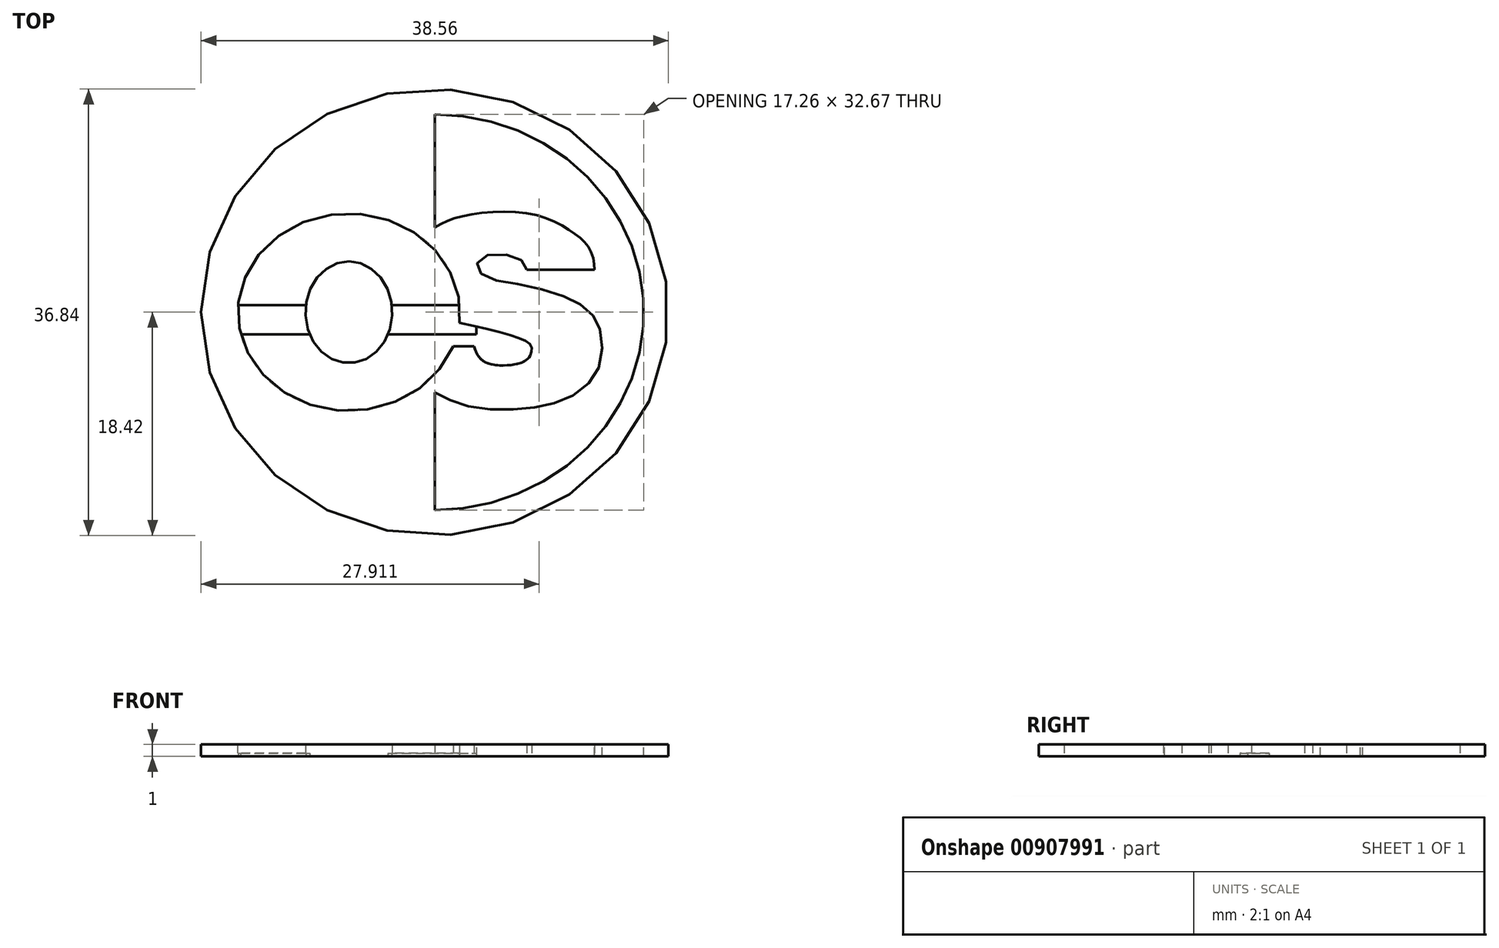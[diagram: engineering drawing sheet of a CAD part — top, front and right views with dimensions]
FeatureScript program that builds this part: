
annotation { "Feature Type Name" : "Feature", "Feature Type Description" : "" }
export const myFeature = defineFeature(function(context is Context, id is Id, definition is map)
    precondition{}
    {
        {
            var Q0;
            Q0=qCreatedBy(makeId("Top.planeOp"),FACE);
            var sketch = newSketch(context, id + "F0", { "sketchPlane" : qUnion([Q0])});
            skEllipse(sketch, "E0", {"center": v(0, 0) * mm, "majorRadius": 18.42 * mm, "minorRadius": 19.28 * mm, "majorAxis": v(0, 1)});
            skEllipticalArc(sketch, "E1", {});
            skEllipse(sketch, "E2", {"center": v(-7.08, 0) * mm, "majorRadius": 4.2 * mm, "minorRadius": 3.58 * mm, "majorAxis": v(0, 1)});
            skEllipticalArc(sketch, "E3", {});
            skLineSegment(sketch, "E4", {"start": v(0, 16.34) * mm, "end": v(0, 6.99) * mm});
            skLineSegment(sketch, "E5", {"start": v(0, -6.61) * mm, "end": v(0, -16.34) * mm});
            skFitSpline(sketch, "E6", {"points": [v(0, 6.99) * mm, v(2.69, 8.01) * mm, v(8.28, 8.04) * mm, v(11.51, 6.51) * mm, v(12.8, 5.2) * mm, v(13.2, 3.52) * mm], "startDerivative": vector(11.6, 7.03) * mm, "endDerivative": vector(-0.27, -9.65) * mm});
            skLineSegment(sketch, "E7", {"start": v(13.2, 3.52) * mm, "end": v(7.61, 3.52) * mm});
            skFitSpline(sketch, "E8", {"points": [v(7.61, 3.52) * mm, v(7.34, 4.12) * mm, v(6.38, 4.64) * mm, v(4.4, 4.73) * mm, v(3.55, 4.12) * mm, v(3.55, 3.52) * mm, v(4.5, 2.8) * mm, v(6.82, 2.34) * mm, v(10.06, 1.51) * mm, v(11.98, 0.66) * mm, v(13.13, -0.38) * mm, v(13.68, -1.53) * mm, v(13.74, -3.81) * mm, v(13, -5.54) * mm, v(11.26, -6.97) * mm, v(9.1, -7.71) * mm, v(6.68, -8.01) * mm, v(3.74, -7.93) * mm, v(1.52, -7.35) * mm, v(0, -6.61) * mm], "startDerivative": vector(-5.92, 19.87) * mm, "endDerivative": vector(-28.15, 15.2) * mm});
            skFitSpline(sketch, "E9", {"points": [v(2.03, -0.88) * mm, v(7.2, -2.24) * mm, v(7.99, -2.84) * mm, v(7.94, -3.44) * mm, v(7.65, -3.89) * mm, v(7.16, -4.16) * mm, v(6.1, -4.37) * mm, v(4.53, -4.26) * mm, v(3.63, -3.67) * mm, v(3.24, -2.8) * mm], "startDerivative": vector(27.73, -5.84) * mm, "endDerivative": vector(-3.04, 9.34) * mm});
            skLineSegment(sketch, "E10", {"start": v(3.24, -2.8) * mm, "end": v(1.52, -2.8) * mm});
            const initialGuessF0  = {"E1": [0, 0, 0, 1, 0.016336938366293907, 0.01726117617026608, 3.141592653589793, 6.283185307179586], "E3": [-0.007082561030983925, 0, 0, 1, 0.008139732798417341, 0.009165805267224644, 4.6041913365112315, 4.36023600412348]};
            skSetInitialGuess(sketch, initialGuessF0);
            skSolve(sketch);
        }
        {
            var Q0;
            Q0=makeQuery(id+"F0.imprint","IMPRINT",FACE,{"disambiguationData":[TD([[makeQuery(id+"F0.imprint","IMPRINT",EDGE,{"derivedFrom":sQuery(id+"F0.wireOp",EDGE,"E0")}),1.0]])]});
            var Q1;
            Q1=makeQuery(id+"F0.imprint","IMPRINT",FACE,{"disambiguationData":[TD([[makeQuery(id+"F0.imprint","IMPRINT",EDGE,{"derivedFrom":sQuery(id+"F0.wireOp",EDGE,"E2")}),1.0]])]});
            extrude(context, id + "F1", {"entities" : qUnion([Q0, Q1]), "depth" : 1 * mm, "offsetDistance" : 25 * mm});
        }
        {
            var Q0;
            Q0=makeQuery(id+"F1.opExtrude","CAP_FACE",FACE,{"disambiguationData":[OSD([sQuery(id+"F0.wireOp",EDGE,"E2")])],"isStart":true});
            var sketch = newSketch(context, id + "F2", { "sketchPlane" : qUnion([Q0])});
            skLineSegment(sketch, "E11", {"start": v(-17, 1.82) * mm, "end": v(3.45, 1.82) * mm});
            skLineSegment(sketch, "E12", {"start": v(3.45, 1.82) * mm, "end": v(3.45, -0.6) * mm});
            skLineSegment(sketch, "E13", {"start": v(3.45, -0.6) * mm, "end": v(-17.06, -0.6) * mm});
            skLineSegment(sketch, "E14", {"start": v(-17.06, -0.6) * mm, "end": v(-17, 1.82) * mm});
            skSolve(sketch);
        }
        {
            var Q0;
            {var subQ0=sQuery(id+"F2.wireOp",EDGE,"E14");Q0=makeQuery(id+"F2.imprint","IMPRINT",FACE,{"disambiguationData":[TD([[makeQuery(id+"F2.imprint","IMPRINT",EDGE,{"derivedFrom":subQ0}),-1.0]])]});}
            var Q1;
            {var subQ0=sQuery(id+"F2.wireOp",EDGE,"E11");var subQ1=makeQuery(id+"F1.opExtrude","CAP_EDGE",EDGE,{"disambiguationData":[OSD([sQuery(id+"F0.wireOp",EDGE,"E2")])],"isStart":false});var subQ2=makeQuery(id+"F2.imprint","INTERSECT",VERTEX,{"disambiguationData":[OD(0.0)],"derivedFrom":[subQ1,subQ0]});Q1=makeQuery(id+"F2.imprint","IMPRINT",FACE,{"disambiguationData":[TD([[makeQuery(id+"F2.imprint","IMPRINT",EDGE,{"disambiguationData":[TD([[subQ2,-1.0]])],"derivedFrom":subQ0}),-1.0]])]});}
            var Q2;
            {var subQ0=sQuery(id+"F2.wireOp",EDGE,"E12");Q2=makeQuery(id+"F2.imprint","IMPRINT",FACE,{"disambiguationData":[TD([[makeQuery(id+"F2.imprint","IMPRINT",EDGE,{"derivedFrom":subQ0}),-1.0]])]});}
            extrude(context, id + "F3", {"entities" : qUnion([Q0, Q1, Q2]), "operationType" : NewBodyOperationType.ADD, "oppositeDirection" : true, "depth" : .25 * mm, "offsetDistance" : 25 * mm});
        }
    });
